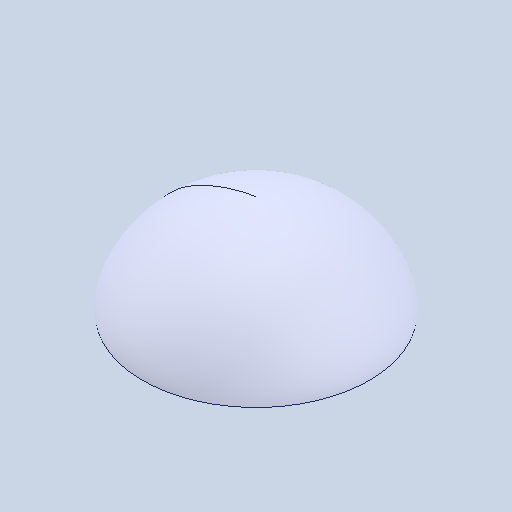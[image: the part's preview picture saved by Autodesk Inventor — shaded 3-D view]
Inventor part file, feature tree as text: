
AUTODESK INVENTOR PART (.ipt)
format: ipt  version: 2024 (Build 280153000, 153)  size: 155,136 bytes
history: native  units: in
note: dims shown in document units (in); Inventor stores cm internally (conversion verified against a paired STEP export)
features: revolve x1
ambient origin geometry x8: Origin, YZ Plane, XZ Plane, XY Plane, X Axis, Y Axis, Z Axis, Center Point
bodies: Solid1 (feature_tree)
feature tree (1):
  revolve  "Revolve1"  [1 undecoded]
note: 1 required parameter value undecoded (feature->parameter linkage not recoverable at this tier; creation-order binding heuristic only, values carry confidence <= 0.55)
